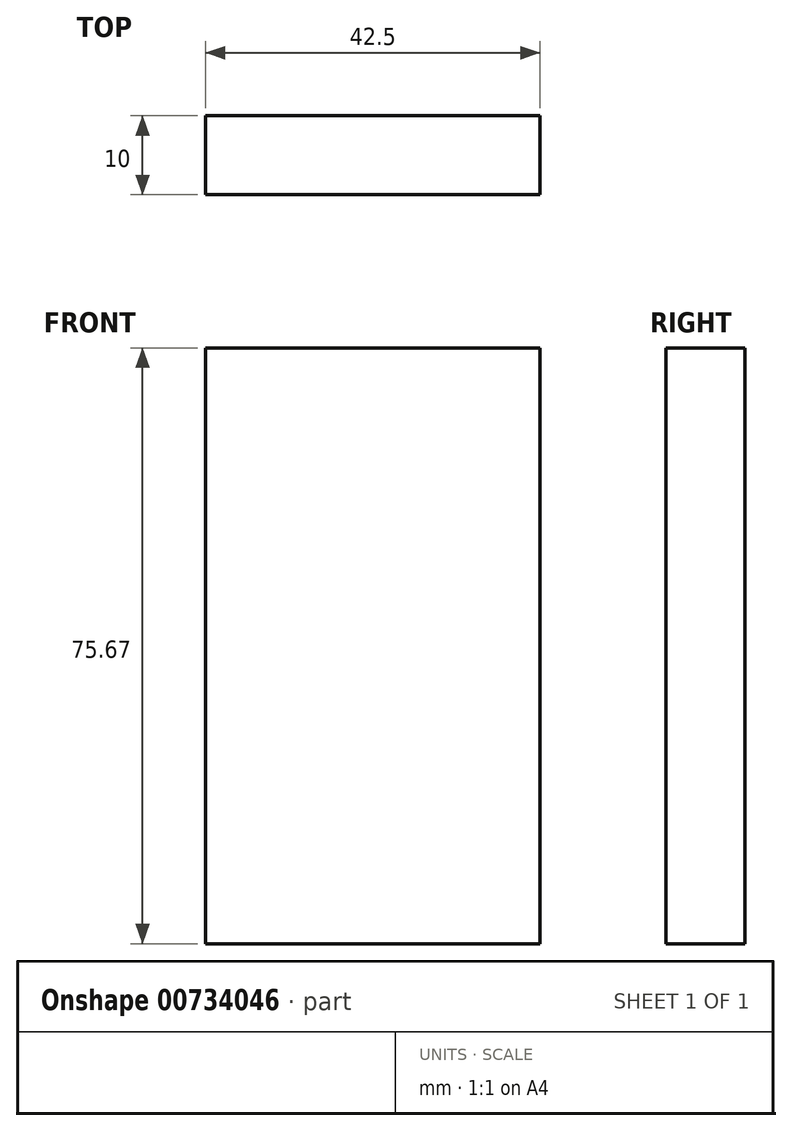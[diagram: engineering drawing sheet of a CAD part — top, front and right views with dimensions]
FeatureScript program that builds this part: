
annotation { "Feature Type Name" : "Feature", "Feature Type Description" : "" }
export const myFeature = defineFeature(function(context is Context, id is Id, definition is map)
    precondition{}
    {
        {
            var Q0;
            Q0=qCreatedBy(makeId("Front.planeOp"),FACE);
            var sketch = newSketch(context, id + "F0", { "sketchPlane" : qUnion([Q0])});
            skLineSegment(sketch, "E0.bottom", {"start": v(-21.25, 42.36) * mm, "end": v(21.25, 42.36) * mm});
            skLineSegment(sketch, "E0.top", {"start": v(-21.25, -33.3) * mm, "end": v(21.25, -33.3) * mm});
            skLineSegment(sketch, "E0.left", {"start": v(-21.25, 42.36) * mm, "end": v(-21.25, -33.3) * mm});
            skLineSegment(sketch, "E0.right", {"start": v(21.25, 42.36) * mm, "end": v(21.25, -33.3) * mm});
            skSolve(sketch);
        }
        {
            var Q0;
            Q0=qSketchRegion(id+"F0",true);
            extrude(context, id + "F1", {"entities" : qUnion([Q0]), "depth" : 10 * mm, "offsetDistance" : 25 * mm});
        }
    });
